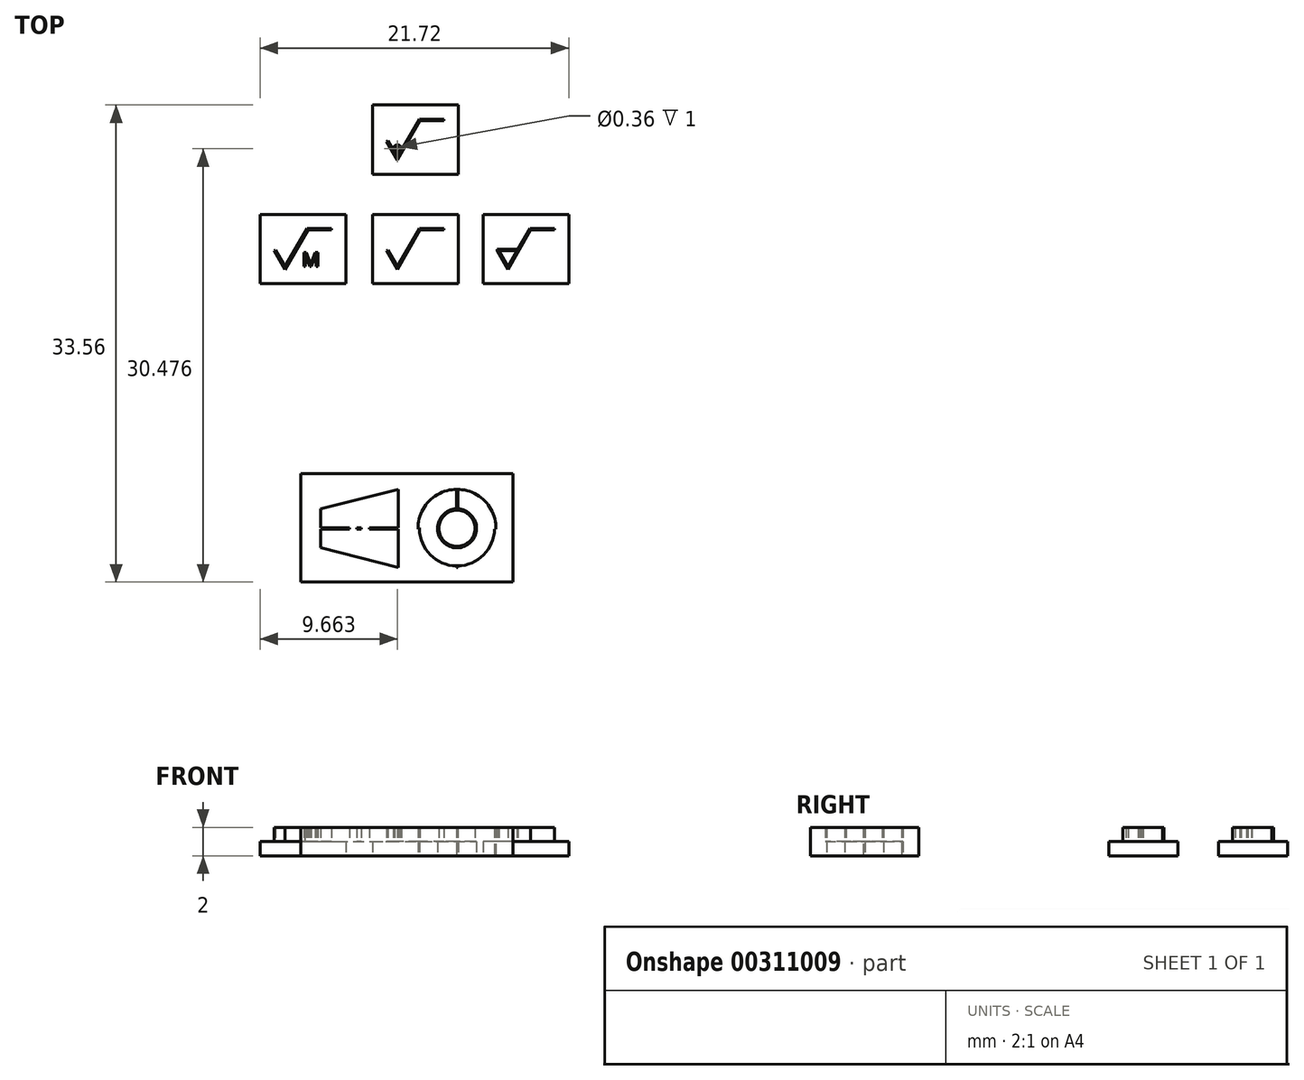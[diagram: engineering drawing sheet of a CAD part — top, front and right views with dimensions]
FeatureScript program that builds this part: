
annotation { "Feature Type Name" : "Feature", "Feature Type Description" : "" }
export const myFeature = defineFeature(function(context is Context, id is Id, definition is map)
    precondition{}
    {
        {
            var Q0;
            Q0=qCreatedBy(makeId("Top.planeOp"),FACE);
            var sketch = newSketch(context, id + "F0", { "sketchPlane" : qUnion([Q0])});
            skLineSegment(sketch, "E0", {"start": v(0, 0) * mm, "end": v(0, 277) * mm});
            skLineSegment(sketch, "E1", {"start": v(0, 277) * mm, "end": v(190, 277) * mm});
            skLineSegment(sketch, "E2", {"start": v(190, 277) * mm, "end": v(190, 0) * mm});
            skLineSegment(sketch, "E3", {"start": v(190, 0) * mm, "end": v(0, 0) * mm});
            skLineSegment(sketch, "E4", {"start": v(43, 0) * mm, "end": v(43, -9.5) * mm});
            skLineSegment(sketch, "E5", {"start": v(43, 277) * mm, "end": v(43, 286.5) * mm});
            skLineSegment(sketch, "E6", {"start": v(95, 0) * mm, "end": v(95, -9.5) * mm});
            skLineSegment(sketch, "E7", {"start": v(95, 277) * mm, "end": v(95, 286.5) * mm});
            skLineSegment(sketch, "E8", {"start": v(147, 0) * mm, "end": v(147, -9.5) * mm});
            skLineSegment(sketch, "E9", {"start": v(147, 277) * mm, "end": v(147, 286.5) * mm});
            skLineSegment(sketch, "E10", {"start": v(0, 40.5) * mm, "end": v(-9.5, 40.5) * mm});
            skLineSegment(sketch, "E11", {"start": v(190, 40.5) * mm, "end": v(199.5, 40.5) * mm});
            skLineSegment(sketch, "E12", {"start": v(0, 89.5) * mm, "end": v(-9.5, 89.5) * mm});
            skLineSegment(sketch, "E13", {"start": v(190, 89.5) * mm, "end": v(199.5, 89.5) * mm});
            skLineSegment(sketch, "E14", {"start": v(0, 138.5) * mm, "end": v(-9.5, 138.5) * mm});
            skLineSegment(sketch, "E15", {"start": v(190, 138.5) * mm, "end": v(199.5, 138.5) * mm});
            skLineSegment(sketch, "E16", {"start": v(0, 187.5) * mm, "end": v(-9.5, 187.5) * mm});
            skLineSegment(sketch, "E17", {"start": v(190, 187.5) * mm, "end": v(199.5, 187.5) * mm});
            skLineSegment(sketch, "E18", {"start": v(0, 236.5) * mm, "end": v(-9.5, 236.5) * mm});
            skLineSegment(sketch, "E19", {"start": v(190, 236.5) * mm, "end": v(199.5, 236.5) * mm});
            skLineSegment(sketch, "E20", {"start": v(28.08, 0) * mm, "end": v(28.08, 38.1) * mm});
            skLineSegment(sketch, "E21", {"start": v(28.08, 0) * mm, "end": v(58.56, 0) * mm});
            skLineSegment(sketch, "E22", {"start": v(28.08, 7.62) * mm, "end": v(58.56, 7.62) * mm});
            skLineSegment(sketch, "E23", {"start": v(28.08, 10.67) * mm, "end": v(58.56, 10.67) * mm});
            skLineSegment(sketch, "E24", {"start": v(28.08, 15.85) * mm, "end": v(58.56, 15.85) * mm});
            skLineSegment(sketch, "E25", {"start": v(28.08, 20.27) * mm, "end": v(58.56, 20.27) * mm});
            skLineSegment(sketch, "E26", {"start": v(28.08, 38.1) * mm, "end": v(58.56, 38.1) * mm});
            skLineSegment(sketch, "E27", {"start": v(41.8, 23.3) * mm, "end": v(42.55, 21.99) * mm});
            skLineSegment(sketch, "E28", {"start": v(42.55, 21.99) * mm, "end": v(44.15, 24.76) * mm});
            skLineSegment(sketch, "E29", {"start": v(44.15, 24.76) * mm, "end": v(45.83, 24.76) * mm});
            skCircle(sketch, "E30", {"center": v(46.74, 3.78) * mm, "radius": 1.37 * mm});
            skCircle(sketch, "E31", {"center": v(46.74, 3.78) * mm, "radius": 2.74 * mm});
            skLineSegment(sketch, "E32", {"start": v(47.43, 3.78) * mm, "end": v(46.06, 3.78) * mm, "construction": true});
            skLineSegment(sketch, "E33", {"start": v(46.74, 4.47) * mm, "end": v(46.74, 3.1) * mm, "construction": true});
            skLineSegment(sketch, "E34", {"start": v(48.12, 3.78) * mm, "end": v(50.17, 3.78) * mm, "construction": true});
            skLineSegment(sketch, "E35", {"start": v(46.74, 5.15) * mm, "end": v(46.74, 7.2) * mm});
            skLineSegment(sketch, "E36", {"start": v(45.37, 3.78) * mm, "end": v(43.31, 3.78) * mm, "construction": true});
            skLineSegment(sketch, "E37", {"start": v(46.74, 2.4) * mm, "end": v(46.74, 0.35) * mm, "construction": true});
            skLineSegment(sketch, "E38", {"start": v(42.63, 1.04) * mm, "end": v(42.63, 6.52) * mm});
            skLineSegment(sketch, "E39", {"start": v(42.63, 6.52) * mm, "end": v(37.14, 5.15) * mm});
            skLineSegment(sketch, "E40", {"start": v(37.14, 5.15) * mm, "end": v(37.14, 2.4) * mm});
            skLineSegment(sketch, "E41", {"start": v(37.14, 2.4) * mm, "end": v(42.63, 1.04) * mm});
            skLineSegment(sketch, "E42", {"start": v(40.57, 3.78) * mm, "end": v(42.97, 3.78) * mm, "construction": true});
            skLineSegment(sketch, "E43", {"start": v(40.02, 3.78) * mm, "end": v(39.68, 3.78) * mm, "construction": true});
            skLineSegment(sketch, "E44", {"start": v(39.2, 3.78) * mm, "end": v(36.8, 3.78) * mm, "construction": true});
            skLineSegment(sketch, "E45", {"start": v(58.56, 0) * mm, "end": v(58.56, 38.1) * mm});
            skLineSegment(sketch, "E46", {"start": v(71.9, 10.67) * mm, "end": v(71.9, 38.1) * mm});
            skLineSegment(sketch, "E47", {"start": v(87.13, 10.67) * mm, "end": v(87.13, 38.1) * mm});
            skLineSegment(sketch, "E48", {"start": v(85.22, 0) * mm, "end": v(85.22, 10.67) * mm});
            skLineSegment(sketch, "E49", {"start": v(102.37, 10.67) * mm, "end": v(102.37, 38.1) * mm});
            skLineSegment(sketch, "E50", {"start": v(58.56, 38.1) * mm, "end": v(111.9, 38.1) * mm});
            skLineSegment(sketch, "E51", {"start": v(58.56, 33.53) * mm, "end": v(111.9, 33.53) * mm});
            skLineSegment(sketch, "E52", {"start": v(58.56, 28.96) * mm, "end": v(111.9, 28.96) * mm});
            skLineSegment(sketch, "E53", {"start": v(58.56, 24.38) * mm, "end": v(111.9, 24.38) * mm});
            skLineSegment(sketch, "E54", {"start": v(58.56, 19.81) * mm, "end": v(111.9, 19.81) * mm});
            skLineSegment(sketch, "E55", {"start": v(58.56, 15.24) * mm, "end": v(111.9, 15.24) * mm});
            skLineSegment(sketch, "E56", {"start": v(58.56, 10.67) * mm, "end": v(111.9, 10.67) * mm});
            skLineSegment(sketch, "E57", {"start": v(111.9, 0) * mm, "end": v(111.9, 38.1) * mm});
            skLineSegment(sketch, "E58", {"start": v(121.42, 4.95) * mm, "end": v(121.42, 12.57) * mm});
            skLineSegment(sketch, "E59", {"start": v(128.66, 0) * mm, "end": v(128.66, 4.95) * mm});
            skLineSegment(sketch, "E60", {"start": v(163.33, 0) * mm, "end": v(163.33, 4.95) * mm});
            skLineSegment(sketch, "E61", {"start": v(182.38, 4.95) * mm, "end": v(182.38, 12.57) * mm});
            skLineSegment(sketch, "E62", {"start": v(111.9, 4.95) * mm, "end": v(190, 4.95) * mm});
            skLineSegment(sketch, "E63", {"start": v(111.9, 12.57) * mm, "end": v(190, 12.57) * mm});
            skLineSegment(sketch, "E64", {"start": v(111.9, 28.58) * mm, "end": v(190, 28.58) * mm});
            skLineSegment(sketch, "E65", {"start": v(111.9, 38.1) * mm, "end": v(190, 38.1) * mm});
            skLineSegment(sketch, "E66.0", {"start": v(42.73, 6.65) * mm, "end": v(37.04, 5.23) * mm});
            skLineSegment(sketch, "E66.1", {"start": v(42.73, 0.9) * mm, "end": v(42.73, 6.65) * mm});
            skLineSegment(sketch, "E66.2", {"start": v(37.04, 2.33) * mm, "end": v(42.73, 0.9) * mm});
            skLineSegment(sketch, "E66.3", {"start": v(37.04, 5.23) * mm, "end": v(37.04, 2.33) * mm});
            skLineSegment(sketch, "E67.bottom", {"start": v(39.2, 3.83) * mm, "end": v(36.8, 3.83) * mm});
            skLineSegment(sketch, "E67.top", {"start": v(39.2, 3.73) * mm, "end": v(36.8, 3.73) * mm});
            skLineSegment(sketch, "E67.left", {"start": v(39.2, 3.83) * mm, "end": v(39.2, 3.73) * mm});
            skLineSegment(sketch, "E67.right", {"start": v(36.8, 3.83) * mm, "end": v(36.8, 3.73) * mm});
            skPoint(sketch, "E67.middle", {"position": v(38, 3.78) * mm});
            skLineSegment(sketch, "E68", {"start": v(35.3, 5.15) * mm, "end": v(35.3, 2.4) * mm, "construction": true});
            skPoint(sketch, "E69", {"position": v(35.3, 3.78) * mm});
            skCircle(sketch, "E70.0", {"center": v(46.74, 3.78) * mm, "radius": 2.64 * mm});
            skCircle(sketch, "E71.0", {"center": v(46.74, 3.78) * mm, "radius": 1.27 * mm});
            skLineSegment(sketch, "E72.bottom", {"start": v(39.68, 3.83) * mm, "end": v(40.02, 3.83) * mm});
            skLineSegment(sketch, "E72.top", {"start": v(39.68, 3.73) * mm, "end": v(40.02, 3.73) * mm});
            skLineSegment(sketch, "E72.left", {"start": v(39.68, 3.83) * mm, "end": v(39.68, 3.73) * mm});
            skLineSegment(sketch, "E72.right", {"start": v(40.02, 3.83) * mm, "end": v(40.02, 3.73) * mm});
            skPoint(sketch, "E72.middle", {"position": v(39.85, 3.78) * mm});
            skLineSegment(sketch, "E73.bottom", {"start": v(42.97, 3.83) * mm, "end": v(40.57, 3.83) * mm});
            skLineSegment(sketch, "E73.top", {"start": v(42.97, 3.73) * mm, "end": v(40.57, 3.73) * mm});
            skLineSegment(sketch, "E73.left", {"start": v(42.97, 3.83) * mm, "end": v(42.97, 3.73) * mm});
            skLineSegment(sketch, "E73.right", {"start": v(40.57, 3.83) * mm, "end": v(40.57, 3.73) * mm});
            skPoint(sketch, "E73.middle", {"position": v(41.77, 3.78) * mm});
            skLineSegment(sketch, "E74.bottom", {"start": v(43.31, 3.83) * mm, "end": v(45.37, 3.83) * mm});
            skLineSegment(sketch, "E74.top", {"start": v(43.31, 3.73) * mm, "end": v(45.37, 3.73) * mm});
            skLineSegment(sketch, "E74.left", {"start": v(43.31, 3.83) * mm, "end": v(43.31, 3.73) * mm});
            skLineSegment(sketch, "E74.right", {"start": v(45.37, 3.83) * mm, "end": v(45.37, 3.73) * mm});
            skPoint(sketch, "E74.middle", {"position": v(44.34, 3.78) * mm});
            skLineSegment(sketch, "E75.bottom", {"start": v(47.43, 3.83) * mm, "end": v(46.06, 3.83) * mm});
            skLineSegment(sketch, "E75.top", {"start": v(47.43, 3.73) * mm, "end": v(46.06, 3.73) * mm});
            skLineSegment(sketch, "E75.left", {"start": v(47.43, 3.83) * mm, "end": v(47.43, 3.73) * mm});
            skLineSegment(sketch, "E75.right", {"start": v(46.06, 3.83) * mm, "end": v(46.06, 3.73) * mm});
            skLineSegment(sketch, "E76.bottom", {"start": v(46.8, 4.47) * mm, "end": v(46.7, 4.47) * mm});
            skLineSegment(sketch, "E76.top", {"start": v(46.8, 3.1) * mm, "end": v(46.7, 3.1) * mm});
            skLineSegment(sketch, "E76.left", {"start": v(46.8, 4.47) * mm, "end": v(46.8, 3.1) * mm});
            skLineSegment(sketch, "E76.right", {"start": v(46.7, 4.47) * mm, "end": v(46.7, 3.1) * mm});
            skLineSegment(sketch, "E77.bottom", {"start": v(46.8, 2.4) * mm, "end": v(46.7, 2.4) * mm});
            skLineSegment(sketch, "E77.top", {"start": v(46.8, 0.35) * mm, "end": v(46.7, 0.35) * mm});
            skLineSegment(sketch, "E77.left", {"start": v(46.8, 2.4) * mm, "end": v(46.8, 0.35) * mm});
            skLineSegment(sketch, "E77.right", {"start": v(46.7, 2.4) * mm, "end": v(46.7, 0.35) * mm});
            skPoint(sketch, "E77.middle", {"position": v(46.74, 1.38) * mm});
            skPoint(sketch, "E78", {"position": v(46.74, 6.18) * mm});
            skLineSegment(sketch, "E79.bottom", {"start": v(46.8, 5.15) * mm, "end": v(46.7, 5.15) * mm});
            skLineSegment(sketch, "E79.top", {"start": v(46.8, 7.2) * mm, "end": v(46.7, 7.2) * mm});
            skLineSegment(sketch, "E79.left", {"start": v(46.8, 5.15) * mm, "end": v(46.8, 7.2) * mm});
            skLineSegment(sketch, "E79.right", {"start": v(46.7, 5.15) * mm, "end": v(46.7, 7.2) * mm});
            skLineSegment(sketch, "E80.bottom", {"start": v(35.77, 7.62) * mm, "end": v(50.68, 7.62) * mm});
            skLineSegment(sketch, "E80.top", {"start": v(35.77, 0) * mm, "end": v(50.68, 0) * mm});
            skLineSegment(sketch, "E80.left", {"start": v(35.77, 7.62) * mm, "end": v(35.77, 0) * mm});
            skLineSegment(sketch, "E80.right", {"start": v(50.68, 7.62) * mm, "end": v(50.68, 0) * mm});
            skLineSegment(sketch, "E81.bottom", {"start": v(48.11, 3.83) * mm, "end": v(50.17, 3.83) * mm});
            skLineSegment(sketch, "E81.top", {"start": v(48.11, 3.73) * mm, "end": v(50.17, 3.73) * mm});
            skLineSegment(sketch, "E81.left", {"start": v(48.11, 3.83) * mm, "end": v(48.11, 3.73) * mm});
            skLineSegment(sketch, "E81.right", {"start": v(50.17, 3.83) * mm, "end": v(50.17, 3.73) * mm});
            skPoint(sketch, "E81.middle", {"position": v(49.14, 3.78) * mm});
            skLineSegment(sketch, "E82", {"start": v(41.8, 23.3) * mm, "end": v(41.88, 23.36) * mm});
            skLineSegment(sketch, "E83", {"start": v(41.88, 23.36) * mm, "end": v(42.55, 22.19) * mm});
            skLineSegment(sketch, "E84", {"start": v(42.55, 22.19) * mm, "end": v(44.15, 24.96) * mm});
            skLineSegment(sketch, "E85", {"start": v(44.15, 24.96) * mm, "end": v(45.83, 24.96) * mm, "construction": true});
            skLineSegment(sketch, "E86", {"start": v(45.83, 24.96) * mm, "end": v(45.83, 24.76) * mm});
            skLineSegment(sketch, "E87", {"start": v(45.83, 24.86) * mm, "end": v(44.1, 24.86) * mm});
            skPoint(sketch, "E88", {"position": v(50.33, 21.99) * mm});
            skLineSegment(sketch, "E89", {"start": v(49.57, 23.3) * mm, "end": v(50.33, 21.99) * mm});
            skLineSegment(sketch, "E90", {"start": v(50.33, 21.99) * mm, "end": v(51.93, 24.76) * mm});
            skLineSegment(sketch, "E91", {"start": v(51.93, 24.76) * mm, "end": v(53.6, 24.76) * mm});
            skLineSegment(sketch, "E92", {"start": v(49.57, 23.3) * mm, "end": v(49.65, 23.36) * mm, "construction": true});
            skLineSegment(sketch, "E93", {"start": v(49.65, 23.36) * mm, "end": v(50.33, 22.19) * mm});
            skLineSegment(sketch, "E94", {"start": v(50.33, 22.19) * mm, "end": v(51.93, 24.96) * mm});
            skLineSegment(sketch, "E95", {"start": v(51.93, 24.96) * mm, "end": v(53.6, 24.96) * mm, "construction": true});
            skLineSegment(sketch, "E96", {"start": v(53.6, 24.96) * mm, "end": v(53.6, 24.76) * mm});
            skLineSegment(sketch, "E97", {"start": v(53.6, 24.86) * mm, "end": v(51.87, 24.86) * mm});
            skPoint(sketch, "E98", {"position": v(49.57, 23.3) * mm});
            skPoint(sketch, "E99", {"position": v(51.1, 23.3) * mm});
            skLineSegment(sketch, "E100.bottom", {"start": v(49.57, 23.3) * mm, "end": v(51.1, 23.3) * mm});
            skLineSegment(sketch, "E100.top", {"start": v(49.57, 23.4) * mm, "end": v(51.1, 23.4) * mm});
            skLineSegment(sketch, "E100.left", {"start": v(49.57, 23.3) * mm, "end": v(49.57, 23.4) * mm});
            skLineSegment(sketch, "E100.right", {"start": v(51.1, 23.3) * mm, "end": v(51.1, 23.4) * mm});
            skPoint(sketch, "E101", {"position": v(40.8, 23.3) * mm});
            skPoint(sketch, "E102", {"position": v(45.83, 23.3) * mm});
            skPoint(sketch, "E103", {"position": v(46.83, 23.3) * mm});
            skPoint(sketch, "E104", {"position": v(42.55, 21.99) * mm});
            skPoint(sketch, "E105", {"position": v(42.55, 20.99) * mm});
            skPoint(sketch, "E106", {"position": v(44.1, 25.86) * mm});
            skLineSegment(sketch, "E107.bottom", {"start": v(40.8, 25.86) * mm, "end": v(46.83, 25.86) * mm});
            skLineSegment(sketch, "E107.top", {"start": v(40.8, 20.99) * mm, "end": v(46.83, 20.99) * mm});
            skLineSegment(sketch, "E107.left", {"start": v(40.8, 25.86) * mm, "end": v(40.8, 20.99) * mm});
            skLineSegment(sketch, "E107.right", {"start": v(46.83, 25.86) * mm, "end": v(46.83, 20.99) * mm});
            skLineSegment(sketch, "E108.bottom", {"start": v(54.6, 25.86) * mm, "end": v(48.57, 25.86) * mm});
            skLineSegment(sketch, "E108.top", {"start": v(54.6, 20.99) * mm, "end": v(48.57, 20.99) * mm});
            skLineSegment(sketch, "E108.left", {"start": v(54.6, 25.86) * mm, "end": v(54.6, 20.99) * mm});
            skLineSegment(sketch, "E108.right", {"start": v(48.57, 25.86) * mm, "end": v(48.57, 20.99) * mm});
            skPoint(sketch, "E109", {"position": v(40.8, 20.99) * mm});
            skLineSegment(sketch, "E110", {"start": v(33.9, 23.3) * mm, "end": v(34.65, 21.99) * mm});
            skLineSegment(sketch, "E111", {"start": v(34.65, 21.99) * mm, "end": v(36.25, 24.76) * mm});
            skLineSegment(sketch, "E112", {"start": v(36.25, 24.76) * mm, "end": v(37.93, 24.76) * mm});
            skLineSegment(sketch, "E113", {"start": v(33.9, 23.3) * mm, "end": v(33.98, 23.36) * mm});
            skLineSegment(sketch, "E114", {"start": v(33.98, 23.36) * mm, "end": v(34.65, 22.19) * mm});
            skLineSegment(sketch, "E115", {"start": v(34.65, 22.19) * mm, "end": v(36.25, 24.96) * mm});
            skLineSegment(sketch, "E116", {"start": v(36.25, 24.96) * mm, "end": v(37.93, 24.96) * mm, "construction": true});
            skLineSegment(sketch, "E117", {"start": v(37.93, 24.96) * mm, "end": v(37.93, 24.76) * mm});
            skLineSegment(sketch, "E118", {"start": v(37.93, 24.86) * mm, "end": v(36.2, 24.86) * mm});
            skPoint(sketch, "E119", {"position": v(32.9, 23.3) * mm});
            skPoint(sketch, "E120", {"position": v(37.93, 23.3) * mm});
            skPoint(sketch, "E121", {"position": v(38.93, 23.3) * mm});
            skPoint(sketch, "E122", {"position": v(34.65, 21.99) * mm});
            skPoint(sketch, "E123", {"position": v(34.65, 20.99) * mm});
            skPoint(sketch, "E124", {"position": v(36.2, 25.86) * mm});
            skLineSegment(sketch, "E125.bottom", {"start": v(32.9, 25.86) * mm, "end": v(38.93, 25.86) * mm});
            skLineSegment(sketch, "E125.top", {"start": v(32.9, 20.99) * mm, "end": v(38.93, 20.99) * mm});
            skLineSegment(sketch, "E125.left", {"start": v(32.9, 25.86) * mm, "end": v(32.9, 20.99) * mm});
            skLineSegment(sketch, "E125.right", {"start": v(38.93, 25.86) * mm, "end": v(38.93, 20.99) * mm});
            skPoint(sketch, "E126", {"position": v(32.9, 20.99) * mm});
            skText(sketch, "E127", { "text": "M", "fontName": "OpenSans-Regular.ttf"});
            skPoint(sketch, "E128", {"position": v(40.8, 28.7) * mm});
            skLineSegment(sketch, "E129", {"start": v(41.8, 31.01) * mm, "end": v(42.55, 29.7) * mm});
            skLineSegment(sketch, "E130", {"start": v(42.55, 29.7) * mm, "end": v(44.15, 32.46) * mm});
            skLineSegment(sketch, "E131", {"start": v(44.15, 32.46) * mm, "end": v(45.83, 32.46) * mm});
            skLineSegment(sketch, "E132", {"start": v(41.8, 31.01) * mm, "end": v(41.88, 31.06) * mm});
            skLineSegment(sketch, "E133", {"start": v(41.88, 31.06) * mm, "end": v(42.55, 29.9) * mm});
            skLineSegment(sketch, "E134", {"start": v(42.55, 29.9) * mm, "end": v(44.15, 32.66) * mm});
            skLineSegment(sketch, "E135", {"start": v(44.15, 32.66) * mm, "end": v(45.83, 32.66) * mm, "construction": true});
            skLineSegment(sketch, "E136", {"start": v(45.83, 32.66) * mm, "end": v(45.83, 32.46) * mm});
            skLineSegment(sketch, "E137", {"start": v(45.83, 32.56) * mm, "end": v(44.1, 32.56) * mm});
            skPoint(sketch, "E138", {"position": v(40.8, 31.01) * mm});
            skPoint(sketch, "E139", {"position": v(45.83, 31.01) * mm});
            skPoint(sketch, "E140", {"position": v(46.83, 31.01) * mm});
            skPoint(sketch, "E141", {"position": v(42.55, 29.7) * mm});
            skPoint(sketch, "E142", {"position": v(42.55, 28.7) * mm});
            skPoint(sketch, "E143", {"position": v(44.1, 33.56) * mm});
            skLineSegment(sketch, "E144.bottom", {"start": v(40.8, 33.56) * mm, "end": v(46.83, 33.56) * mm});
            skLineSegment(sketch, "E144.top", {"start": v(40.8, 28.7) * mm, "end": v(46.83, 28.7) * mm});
            skLineSegment(sketch, "E144.left", {"start": v(40.8, 33.56) * mm, "end": v(40.8, 28.7) * mm});
            skLineSegment(sketch, "E144.right", {"start": v(46.83, 33.56) * mm, "end": v(46.83, 28.7) * mm});
            skCircle(sketch, "E145", {"center": v(42.55, 30.48) * mm, "radius": 0.28 * mm});
            skPoint(sketch, "E145.centerSnap0", {"position": v(42.22, 30.48) * mm});
            skCircle(sketch, "E146", {"center": v(42.55, 30.48) * mm, "radius": 0.18 * mm});
            skPoint(sketch, "E147", {"position": v(42.8, 30.33) * mm});
            skLineSegment(sketch, "E148", {"start": v(42.44, 30.1) * mm, "end": v(42.55, 29.91) * mm});
            skLineSegment(sketch, "E149", {"start": v(42.55, 29.91) * mm, "end": v(42.68, 30.14) * mm});
            skLineSegment(sketch, "E150", {"start": v(42.55, 29.91) * mm, "end": v(43.07, 30.8) * mm, "construction": true});
            skLineSegment(sketch, "E151", {"start": v(42.55, 29.91) * mm, "end": v(42.12, 30.67) * mm, "construction": true});
            const initialGuessF0  = {"E127": [0.03583, 0.02219, 1, 0, 0.001]};
            skSetInitialGuess(sketch, initialGuessF0);
            skSolve(sketch);
        }
        {
            var Q0;
            {var subQ0=sQuery(id+"F0.wireOp",EDGE,"E79.left");var subQ5=sQuery(id+"F0.wireOp",EDGE,"E70.0");var subQ6=makeQuery(id+"F0.imprint","INTERSECT",VERTEX,{"derivedFrom":[subQ5,subQ0]});Q0=makeQuery(id+"F0.imprint","IMPRINT",FACE,{"disambiguationData":[TD([[makeQuery(id+"F0.imprint","IMPRINT",EDGE,{"disambiguationData":[TD([[subQ6,-1.0]])],"derivedFrom":subQ5}),-1.0]])]});}
            var Q1;
            Q1=makeQuery(id+"F0.imprint","IMPRINT",FACE,{"disambiguationData":[TD([[makeQuery(id+"F0.imprint","IMPRINT",EDGE,{"derivedFrom":sQuery(id+"F0.wireOp",EDGE,"E71.0")}),-1.0]])]});
            var Q2;
            {var subQ1=sQuery(id+"F0.wireOp",EDGE,"E74.bottom");var subQ5=sQuery(id+"F0.wireOp",EDGE,"E70.0");var subQ6=makeQuery(id+"F0.imprint","INTERSECT",VERTEX,{"derivedFrom":[subQ5,subQ1]});Q2=makeQuery(id+"F0.imprint","IMPRINT",FACE,{"disambiguationData":[TD([[makeQuery(id+"F0.imprint","IMPRINT",EDGE,{"disambiguationData":[TD([[subQ6,-1.0]])],"derivedFrom":subQ5}),-1.0]])]});}
            var Q3;
            {var subQ13=sQuery(id+"F0.wireOp",EDGE,"E39");Q3=makeQuery(id+"F0.imprint","IMPRINT",FACE,{"disambiguationData":[TD([[makeQuery(id+"F0.imprint","IMPRINT",EDGE,{"derivedFrom":subQ13}),1.0]])]});}
            var Q4;
            {var subQ0=sQuery(id+"F0.wireOp",EDGE,"E77.left");var subQ5=sQuery(id+"F0.wireOp",EDGE,"E70.0");var subQ6=makeQuery(id+"F0.imprint","INTERSECT",VERTEX,{"derivedFrom":[subQ5,subQ0]});Q4=makeQuery(id+"F0.imprint","IMPRINT",FACE,{"disambiguationData":[TD([[makeQuery(id+"F0.imprint","IMPRINT",EDGE,{"disambiguationData":[TD([[subQ6,1.0]])],"derivedFrom":subQ5}),-1.0]])]});}
            var Q5;
            {var subQ3=sQuery(id+"F0.wireOp",EDGE,"E30");var subQ9=sQuery(id+"F0.wireOp",EDGE,"E77.bottom");var subQ10=makeQuery(id+"F0.imprint","INTERSECT",VERTEX,{"derivedFrom":[subQ3,subQ9]});Q5=makeQuery(id+"F0.imprint","IMPRINT",FACE,{"disambiguationData":[TD([[makeQuery(id+"F0.imprint","IMPRINT",EDGE,{"disambiguationData":[TD([[subQ10,-1.0]])],"derivedFrom":subQ3}),1.0]])]});}
            var Q6;
            {var subQ1=sQuery(id+"F0.wireOp",EDGE,"E74.top");var subQ3=sQuery(id+"F0.wireOp",EDGE,"E70.0");var subQ4=makeQuery(id+"F0.imprint","INTERSECT",VERTEX,{"derivedFrom":[subQ3,subQ1]});Q6=makeQuery(id+"F0.imprint","IMPRINT",FACE,{"disambiguationData":[TD([[makeQuery(id+"F0.imprint","IMPRINT",EDGE,{"disambiguationData":[TD([[subQ4,-1.0]])],"derivedFrom":subQ3}),-1.0]])]});}
            var Q7;
            {var subQ0=sQuery(id+"F0.wireOp",EDGE,"E77.left");var subQ1=sQuery(id+"F0.wireOp",EDGE,"E31");var subQ2=makeQuery(id+"F0.imprint","INTERSECT",VERTEX,{"derivedFrom":[subQ1,subQ0]});Q7=makeQuery(id+"F0.imprint","IMPRINT",FACE,{"disambiguationData":[TD([[makeQuery(id+"F0.imprint","IMPRINT",EDGE,{"disambiguationData":[TD([[subQ2,1.0]])],"derivedFrom":subQ1}),-1.0]])]});}
            var Q8;
            {var subQ0=sQuery(id+"F0.wireOp",EDGE,"E74.bottom");var subQ1=sQuery(id+"F0.wireOp",EDGE,"E31");var subQ2=makeQuery(id+"F0.imprint","INTERSECT",VERTEX,{"derivedFrom":[subQ1,subQ0]});Q8=makeQuery(id+"F0.imprint","IMPRINT",FACE,{"disambiguationData":[TD([[makeQuery(id+"F0.imprint","IMPRINT",EDGE,{"disambiguationData":[TD([[subQ2,-1.0]])],"derivedFrom":subQ1}),-1.0]])]});}
            var Q9;
            {var subQ0=sQuery(id+"F0.wireOp",EDGE,"E67.bottom");var subQ1=sQuery(id+"F0.wireOp",EDGE,"E40");var subQ2=makeQuery(id+"F0.imprint","INTERSECT",VERTEX,{"derivedFrom":[subQ1,subQ0]});Q9=makeQuery(id+"F0.imprint","IMPRINT",FACE,{"disambiguationData":[TD([[makeQuery(id+"F0.imprint","IMPRINT",EDGE,{"disambiguationData":[TD([[subQ2,-1.0]])],"derivedFrom":subQ1}),-1.0]])]});}
            var Q10;
            {var subQ5=sQuery(id+"F0.wireOp",EDGE,"E74.left");Q10=makeQuery(id+"F0.imprint","IMPRINT",FACE,{"disambiguationData":[TD([[makeQuery(id+"F0.imprint","IMPRINT",EDGE,{"derivedFrom":subQ5}),1.0]])]});}
            var Q11;
            {var subQ1=sQuery(id+"F0.wireOp",EDGE,"E79.top");Q11=makeQuery(id+"F0.imprint","IMPRINT",FACE,{"disambiguationData":[TD([[makeQuery(id+"F0.imprint","IMPRINT",EDGE,{"derivedFrom":subQ1}),1.0]])]});}
            var Q12;
            {var subQ0=sQuery(id+"F0.wireOp",EDGE,"E35");var subQ1=sQuery(id+"F0.wireOp",EDGE,"E30");var subQ2=makeQuery(id+"F0.imprint","INTERSECT",VERTEX,{"derivedFrom":[subQ1,subQ0]});Q12=makeQuery(id+"F0.imprint","IMPRINT",FACE,{"disambiguationData":[TD([[makeQuery(id+"F0.imprint","IMPRINT",EDGE,{"disambiguationData":[TD([[subQ2,-1.0]])],"derivedFrom":subQ0}),1.0]])]});}
            var Q13;
            {var subQ0=sQuery(id+"F0.wireOp",EDGE,"E77.left");var subQ3=sQuery(id+"F0.wireOp",EDGE,"E70.0");var subQ4=makeQuery(id+"F0.imprint","INTERSECT",VERTEX,{"derivedFrom":[subQ3,subQ0]});Q13=makeQuery(id+"F0.imprint","IMPRINT",FACE,{"disambiguationData":[TD([[makeQuery(id+"F0.imprint","IMPRINT",EDGE,{"disambiguationData":[TD([[subQ4,-1.0]])],"derivedFrom":subQ3}),-1.0]])]});}
            var Q14;
            Q14=makeQuery(id+"F0.imprint","IMPRINT",FACE,{"disambiguationData":[TD([[makeQuery(id+"F0.imprint","IMPRINT",EDGE,{"derivedFrom":sQuery(id+"F0.wireOp",EDGE,"E71.0")}),1.0]])]});
            var Q15;
            {var subQ4=sQuery(id+"F0.wireOp",EDGE,"E81.top");var subQ6=sQuery(id+"F0.wireOp",EDGE,"E70.0");var subQ7=makeQuery(id+"F0.imprint","INTERSECT",VERTEX,{"derivedFrom":[subQ6,subQ4]});Q15=makeQuery(id+"F0.imprint","IMPRINT",FACE,{"disambiguationData":[TD([[makeQuery(id+"F0.imprint","IMPRINT",EDGE,{"disambiguationData":[TD([[subQ7,1.0]])],"derivedFrom":subQ6}),-1.0]])]});}
            var Q16;
            {var subQ0=sQuery(id+"F0.wireOp",EDGE,"E79.left");var subQ1=sQuery(id+"F0.wireOp",EDGE,"E31");var subQ2=makeQuery(id+"F0.imprint","INTERSECT",VERTEX,{"derivedFrom":[subQ1,subQ0]});Q16=makeQuery(id+"F0.imprint","IMPRINT",FACE,{"disambiguationData":[TD([[makeQuery(id+"F0.imprint","IMPRINT",EDGE,{"disambiguationData":[TD([[subQ2,-1.0]])],"derivedFrom":subQ1}),-1.0]])]});}
            var Q17;
            {var subQ0=sQuery(id+"F0.wireOp",EDGE,"E73.top");var subQ1=sQuery(id+"F0.wireOp",EDGE,"E38");var subQ2=makeQuery(id+"F0.imprint","INTERSECT",VERTEX,{"derivedFrom":[subQ1,subQ0]});Q17=makeQuery(id+"F0.imprint","IMPRINT",FACE,{"disambiguationData":[TD([[makeQuery(id+"F0.imprint","IMPRINT",EDGE,{"disambiguationData":[TD([[subQ2,-1.0]])],"derivedFrom":subQ1}),-1.0]])]});}
            var Q18;
            {var subQ0=sQuery(id+"F0.wireOp",EDGE,"E77.right");var subQ1=sQuery(id+"F0.wireOp",EDGE,"E31");var subQ2=makeQuery(id+"F0.imprint","INTERSECT",VERTEX,{"derivedFrom":[subQ1,subQ0]});Q18=makeQuery(id+"F0.imprint","IMPRINT",FACE,{"disambiguationData":[TD([[makeQuery(id+"F0.imprint","IMPRINT",EDGE,{"disambiguationData":[TD([[subQ2,-1.0]])],"derivedFrom":subQ1}),-1.0]])]});}
            var Q19;
            {var subQ1=sQuery(id+"F0.wireOp",EDGE,"E39");Q19=makeQuery(id+"F0.imprint","IMPRINT",FACE,{"disambiguationData":[TD([[makeQuery(id+"F0.imprint","IMPRINT",EDGE,{"derivedFrom":subQ1}),-1.0]])]});}
            var Q20;
            {var subQ0=sQuery(id+"F0.wireOp",EDGE,"E75.left");Q20=makeQuery(id+"F0.imprint","IMPRINT",FACE,{"disambiguationData":[TD([[makeQuery(id+"F0.imprint","IMPRINT",EDGE,{"derivedFrom":subQ0}),-1.0]])]});}
            var Q21;
            {var subQ5=sQuery(id+"F0.wireOp",EDGE,"E67.left");Q21=makeQuery(id+"F0.imprint","IMPRINT",FACE,{"disambiguationData":[TD([[makeQuery(id+"F0.imprint","IMPRINT",EDGE,{"derivedFrom":subQ5}),-1.0]])]});}
            var Q22;
            {var subQ5=sQuery(id+"F0.wireOp",EDGE,"E73.right");Q22=makeQuery(id+"F0.imprint","IMPRINT",FACE,{"disambiguationData":[TD([[makeQuery(id+"F0.imprint","IMPRINT",EDGE,{"derivedFrom":subQ5}),1.0]])]});}
            var Q23;
            {var subQ5=sQuery(id+"F0.wireOp",EDGE,"E81.right");Q23=makeQuery(id+"F0.imprint","IMPRINT",FACE,{"disambiguationData":[TD([[makeQuery(id+"F0.imprint","IMPRINT",EDGE,{"derivedFrom":subQ5}),-1.0]])]});}
            var Q24;
            {var subQ0=sQuery(id+"F0.wireOp",EDGE,"E41");Q24=makeQuery(id+"F0.imprint","IMPRINT",FACE,{"disambiguationData":[TD([[makeQuery(id+"F0.imprint","IMPRINT",EDGE,{"derivedFrom":subQ0}),-1.0]])]});}
            var Q25;
            {var subQ0=sQuery(id+"F0.wireOp",EDGE,"E35");var subQ1=sQuery(id+"F0.wireOp",EDGE,"E30");var subQ2=makeQuery(id+"F0.imprint","INTERSECT",VERTEX,{"derivedFrom":[subQ1,subQ0]});Q25=makeQuery(id+"F0.imprint","IMPRINT",FACE,{"disambiguationData":[TD([[makeQuery(id+"F0.imprint","IMPRINT",EDGE,{"disambiguationData":[TD([[subQ2,-1.0]])],"derivedFrom":subQ0}),-1.0]])]});}
            var Q26;
            {var subQ0=sQuery(id+"F0.wireOp",EDGE,"E35");var subQ1=sQuery(id+"F0.wireOp",EDGE,"E31");var subQ2=makeQuery(id+"F0.imprint","INTERSECT",VERTEX,{"derivedFrom":[subQ1,subQ0]});Q26=makeQuery(id+"F0.imprint","IMPRINT",FACE,{"disambiguationData":[TD([[makeQuery(id+"F0.imprint","IMPRINT",EDGE,{"disambiguationData":[TD([[subQ2,1.0]])],"derivedFrom":subQ1}),-1.0]])]});}
            var Q27;
            {var subQ5=sQuery(id+"F0.wireOp",EDGE,"E77.top");Q27=makeQuery(id+"F0.imprint","IMPRINT",FACE,{"disambiguationData":[TD([[makeQuery(id+"F0.imprint","IMPRINT",EDGE,{"derivedFrom":subQ5}),-1.0]])]});}
            var Q28;
            {var subQ0=sQuery(id+"F0.wireOp",EDGE,"E81.top");var subQ1=sQuery(id+"F0.wireOp",EDGE,"E31");var subQ2=makeQuery(id+"F0.imprint","INTERSECT",VERTEX,{"derivedFrom":[subQ1,subQ0]});Q28=makeQuery(id+"F0.imprint","IMPRINT",FACE,{"disambiguationData":[TD([[makeQuery(id+"F0.imprint","IMPRINT",EDGE,{"disambiguationData":[TD([[subQ2,1.0]])],"derivedFrom":subQ1}),-1.0]])]});}
            var Q29;
            {var subQ0=sQuery(id+"F0.wireOp",EDGE,"E77.left");var subQ1=sQuery(id+"F0.wireOp",EDGE,"E31");var subQ2=makeQuery(id+"F0.imprint","INTERSECT",VERTEX,{"derivedFrom":[subQ1,subQ0]});Q29=makeQuery(id+"F0.imprint","IMPRINT",FACE,{"disambiguationData":[TD([[makeQuery(id+"F0.imprint","IMPRINT",EDGE,{"disambiguationData":[TD([[subQ2,-1.0]])],"derivedFrom":subQ1}),-1.0]])]});}
            var Q30;
            {var subQ5=sQuery(id+"F0.wireOp",EDGE,"E73.left");Q30=makeQuery(id+"F0.imprint","IMPRINT",FACE,{"disambiguationData":[TD([[makeQuery(id+"F0.imprint","IMPRINT",EDGE,{"derivedFrom":subQ5}),-1.0]])]});}
            var Q31;
            {var subQ5=sQuery(id+"F0.wireOp",EDGE,"E76.top");Q31=makeQuery(id+"F0.imprint","IMPRINT",FACE,{"disambiguationData":[TD([[makeQuery(id+"F0.imprint","IMPRINT",EDGE,{"derivedFrom":subQ5}),-1.0]])]});}
            var Q32;
            {var subQ0=sQuery(id+"F0.wireOp",EDGE,"E74.top");var subQ1=sQuery(id+"F0.wireOp",EDGE,"E31");var subQ2=makeQuery(id+"F0.imprint","INTERSECT",VERTEX,{"derivedFrom":[subQ1,subQ0]});Q32=makeQuery(id+"F0.imprint","IMPRINT",FACE,{"disambiguationData":[TD([[makeQuery(id+"F0.imprint","IMPRINT",EDGE,{"disambiguationData":[TD([[subQ2,-1.0]])],"derivedFrom":subQ1}),-1.0]])]});}
            var Q33;
            {var subQ5=sQuery(id+"F0.wireOp",EDGE,"E76.bottom");Q33=makeQuery(id+"F0.imprint","IMPRINT",FACE,{"disambiguationData":[TD([[makeQuery(id+"F0.imprint","IMPRINT",EDGE,{"derivedFrom":subQ5}),1.0]])]});}
            var Q34;
            {var subQ0=sQuery(id+"F0.wireOp",EDGE,"E35");var subQ1=sQuery(id+"F0.wireOp",EDGE,"E31");var subQ2=makeQuery(id+"F0.imprint","INTERSECT",VERTEX,{"derivedFrom":[subQ1,subQ0]});Q34=makeQuery(id+"F0.imprint","IMPRINT",FACE,{"disambiguationData":[TD([[makeQuery(id+"F0.imprint","IMPRINT",EDGE,{"disambiguationData":[TD([[subQ2,-1.0]])],"derivedFrom":subQ1}),-1.0]])]});}
            var Q35;
            {var subQ5=sQuery(id+"F0.wireOp",EDGE,"E67.right");Q35=makeQuery(id+"F0.imprint","IMPRINT",FACE,{"disambiguationData":[TD([[makeQuery(id+"F0.imprint","IMPRINT",EDGE,{"derivedFrom":subQ5}),1.0]])]});}
            var Q36;
            {var subQ0=sQuery(id+"F0.wireOp",EDGE,"E75.right");Q36=makeQuery(id+"F0.imprint","IMPRINT",FACE,{"disambiguationData":[TD([[makeQuery(id+"F0.imprint","IMPRINT",EDGE,{"derivedFrom":subQ0}),1.0]])]});}
            var Q37;
            {var subQ2=sQuery(id+"F0.wireOp",EDGE,"E79.bottom");Q37=makeQuery(id+"F0.imprint","IMPRINT",FACE,{"disambiguationData":[TD([[makeQuery(id+"F0.imprint","IMPRINT",EDGE,{"derivedFrom":subQ2}),-1.0]])]});}
            var Q38;
            {var subQ0=sQuery(id+"F0.wireOp",EDGE,"E81.left");Q38=makeQuery(id+"F0.imprint","IMPRINT",FACE,{"disambiguationData":[TD([[makeQuery(id+"F0.imprint","IMPRINT",EDGE,{"derivedFrom":subQ0}),1.0]])]});}
            var Q39;
            Q39=makeQuery(id+"F0.imprint","IMPRINT",FACE,{"disambiguationData":[TD([[makeQuery(id+"F0.imprint","IMPRINT",EDGE,{"derivedFrom":sQuery(id+"F0.wireOp",EDGE,"E72.bottom")}),-1.0]])]});
            var Q40;
            {var subQ0=sQuery(id+"F0.wireOp",EDGE,"E76.left");var subQ1=sQuery(id+"F0.wireOp",EDGE,"E75.bottom");var subQ2=makeQuery(id+"F0.imprint","INTERSECT",VERTEX,{"derivedFrom":[subQ1,subQ0]});Q40=makeQuery(id+"F0.imprint","IMPRINT",FACE,{"disambiguationData":[TD([[makeQuery(id+"F0.imprint","IMPRINT",EDGE,{"disambiguationData":[TD([[subQ2,-1.0]])],"derivedFrom":subQ1}),1.0]])]});}
            var Q41;
            {var subQ28=sQuery(id+"F0.wireOp",EDGE,"E66.0");Q41=makeQuery(id+"F0.imprint","IMPRINT",FACE,{"disambiguationData":[TD([[makeQuery(id+"F0.imprint","IMPRINT",EDGE,{"derivedFrom":subQ28}),-1.0]])]});}
            extrude(context, id + "F1", {"entities" : qUnion([Q0, Q1, Q2, Q3, Q4, Q5, Q6, Q7, Q8, Q9, Q10, Q11, Q12, Q13, Q14, Q15, Q16, Q17, Q18, Q19, Q20, Q21, Q22, Q23, Q24, Q25, Q26, Q27, Q28, Q29, Q30, Q31, Q32, Q33, Q34, Q35, Q36, Q37, Q38, Q39, Q40, Q41]), "depth" : 1 * mm});
        }
        {
            var Q0;
            {var subQ0=sQuery(id+"F0.wireOp",EDGE,"E41");Q0=makeQuery(id+"F0.imprint","IMPRINT",FACE,{"disambiguationData":[TD([[makeQuery(id+"F0.imprint","IMPRINT",EDGE,{"derivedFrom":subQ0}),-1.0]])]});}
            var Q1;
            {var subQ1=sQuery(id+"F0.wireOp",EDGE,"E39");Q1=makeQuery(id+"F0.imprint","IMPRINT",FACE,{"disambiguationData":[TD([[makeQuery(id+"F0.imprint","IMPRINT",EDGE,{"derivedFrom":subQ1}),-1.0]])]});}
            var Q2;
            {var subQ5=sQuery(id+"F0.wireOp",EDGE,"E73.right");Q2=makeQuery(id+"F0.imprint","IMPRINT",FACE,{"disambiguationData":[TD([[makeQuery(id+"F0.imprint","IMPRINT",EDGE,{"derivedFrom":subQ5}),1.0]])]});}
            var Q3;
            {var subQ5=sQuery(id+"F0.wireOp",EDGE,"E73.left");Q3=makeQuery(id+"F0.imprint","IMPRINT",FACE,{"disambiguationData":[TD([[makeQuery(id+"F0.imprint","IMPRINT",EDGE,{"derivedFrom":subQ5}),-1.0]])]});}
            var Q4;
            {var subQ0=sQuery(id+"F0.wireOp",EDGE,"E73.top");var subQ1=sQuery(id+"F0.wireOp",EDGE,"E38");var subQ2=makeQuery(id+"F0.imprint","INTERSECT",VERTEX,{"derivedFrom":[subQ1,subQ0]});Q4=makeQuery(id+"F0.imprint","IMPRINT",FACE,{"disambiguationData":[TD([[makeQuery(id+"F0.imprint","IMPRINT",EDGE,{"disambiguationData":[TD([[subQ2,-1.0]])],"derivedFrom":subQ1}),-1.0]])]});}
            var Q5;
            {var subQ5=sQuery(id+"F0.wireOp",EDGE,"E67.left");Q5=makeQuery(id+"F0.imprint","IMPRINT",FACE,{"disambiguationData":[TD([[makeQuery(id+"F0.imprint","IMPRINT",EDGE,{"derivedFrom":subQ5}),-1.0]])]});}
            var Q6;
            {var subQ0=sQuery(id+"F0.wireOp",EDGE,"E67.bottom");var subQ1=sQuery(id+"F0.wireOp",EDGE,"E40");var subQ2=makeQuery(id+"F0.imprint","INTERSECT",VERTEX,{"derivedFrom":[subQ1,subQ0]});Q6=makeQuery(id+"F0.imprint","IMPRINT",FACE,{"disambiguationData":[TD([[makeQuery(id+"F0.imprint","IMPRINT",EDGE,{"disambiguationData":[TD([[subQ2,-1.0]])],"derivedFrom":subQ1}),-1.0]])]});}
            var Q7;
            {var subQ5=sQuery(id+"F0.wireOp",EDGE,"E67.right");Q7=makeQuery(id+"F0.imprint","IMPRINT",FACE,{"disambiguationData":[TD([[makeQuery(id+"F0.imprint","IMPRINT",EDGE,{"derivedFrom":subQ5}),1.0]])]});}
            var Q8;
            Q8=makeQuery(id+"F0.imprint","IMPRINT",FACE,{"disambiguationData":[TD([[makeQuery(id+"F0.imprint","IMPRINT",EDGE,{"derivedFrom":sQuery(id+"F0.wireOp",EDGE,"E72.bottom")}),-1.0]])]});
            var Q9;
            Q9=makeQuery(id+"F0.imprint","IMPRINT",FACE,{"disambiguationData":[TD([[makeQuery(id+"F0.imprint","IMPRINT",EDGE,{"derivedFrom":sQuery(id+"F0.wireOp",EDGE,"E71.0")}),1.0]])]});
            var Q10;
            {var subQ1=sQuery(id+"F0.wireOp",EDGE,"E74.top");var subQ3=sQuery(id+"F0.wireOp",EDGE,"E70.0");var subQ4=makeQuery(id+"F0.imprint","INTERSECT",VERTEX,{"derivedFrom":[subQ3,subQ1]});Q10=makeQuery(id+"F0.imprint","IMPRINT",FACE,{"disambiguationData":[TD([[makeQuery(id+"F0.imprint","IMPRINT",EDGE,{"disambiguationData":[TD([[subQ4,-1.0]])],"derivedFrom":subQ3}),-1.0]])]});}
            var Q11;
            {var subQ0=sQuery(id+"F0.wireOp",EDGE,"E74.top");var subQ1=sQuery(id+"F0.wireOp",EDGE,"E31");var subQ2=makeQuery(id+"F0.imprint","INTERSECT",VERTEX,{"derivedFrom":[subQ1,subQ0]});Q11=makeQuery(id+"F0.imprint","IMPRINT",FACE,{"disambiguationData":[TD([[makeQuery(id+"F0.imprint","IMPRINT",EDGE,{"disambiguationData":[TD([[subQ2,-1.0]])],"derivedFrom":subQ1}),-1.0]])]});}
            var Q12;
            {var subQ5=sQuery(id+"F0.wireOp",EDGE,"E74.left");Q12=makeQuery(id+"F0.imprint","IMPRINT",FACE,{"disambiguationData":[TD([[makeQuery(id+"F0.imprint","IMPRINT",EDGE,{"derivedFrom":subQ5}),1.0]])]});}
            var Q13;
            {var subQ0=sQuery(id+"F0.wireOp",EDGE,"E74.bottom");var subQ1=sQuery(id+"F0.wireOp",EDGE,"E31");var subQ2=makeQuery(id+"F0.imprint","INTERSECT",VERTEX,{"derivedFrom":[subQ1,subQ0]});Q13=makeQuery(id+"F0.imprint","IMPRINT",FACE,{"disambiguationData":[TD([[makeQuery(id+"F0.imprint","IMPRINT",EDGE,{"disambiguationData":[TD([[subQ2,-1.0]])],"derivedFrom":subQ1}),-1.0]])]});}
            var Q14;
            {var subQ0=sQuery(id+"F0.wireOp",EDGE,"E77.left");var subQ1=sQuery(id+"F0.wireOp",EDGE,"E31");var subQ2=makeQuery(id+"F0.imprint","INTERSECT",VERTEX,{"derivedFrom":[subQ1,subQ0]});Q14=makeQuery(id+"F0.imprint","IMPRINT",FACE,{"disambiguationData":[TD([[makeQuery(id+"F0.imprint","IMPRINT",EDGE,{"disambiguationData":[TD([[subQ2,-1.0]])],"derivedFrom":subQ1}),-1.0]])]});}
            var Q15;
            {var subQ0=sQuery(id+"F0.wireOp",EDGE,"E77.right");var subQ1=sQuery(id+"F0.wireOp",EDGE,"E31");var subQ2=makeQuery(id+"F0.imprint","INTERSECT",VERTEX,{"derivedFrom":[subQ1,subQ0]});Q15=makeQuery(id+"F0.imprint","IMPRINT",FACE,{"disambiguationData":[TD([[makeQuery(id+"F0.imprint","IMPRINT",EDGE,{"disambiguationData":[TD([[subQ2,-1.0]])],"derivedFrom":subQ1}),-1.0]])]});}
            var Q16;
            {var subQ0=sQuery(id+"F0.wireOp",EDGE,"E77.left");var subQ1=sQuery(id+"F0.wireOp",EDGE,"E31");var subQ2=makeQuery(id+"F0.imprint","INTERSECT",VERTEX,{"derivedFrom":[subQ1,subQ0]});Q16=makeQuery(id+"F0.imprint","IMPRINT",FACE,{"disambiguationData":[TD([[makeQuery(id+"F0.imprint","IMPRINT",EDGE,{"disambiguationData":[TD([[subQ2,1.0]])],"derivedFrom":subQ1}),-1.0]])]});}
            var Q17;
            {var subQ0=sQuery(id+"F0.wireOp",EDGE,"E77.left");var subQ3=sQuery(id+"F0.wireOp",EDGE,"E70.0");var subQ4=makeQuery(id+"F0.imprint","INTERSECT",VERTEX,{"derivedFrom":[subQ3,subQ0]});Q17=makeQuery(id+"F0.imprint","IMPRINT",FACE,{"disambiguationData":[TD([[makeQuery(id+"F0.imprint","IMPRINT",EDGE,{"disambiguationData":[TD([[subQ4,-1.0]])],"derivedFrom":subQ3}),-1.0]])]});}
            var Q18;
            {var subQ0=sQuery(id+"F0.wireOp",EDGE,"E79.left");var subQ1=sQuery(id+"F0.wireOp",EDGE,"E31");var subQ2=makeQuery(id+"F0.imprint","INTERSECT",VERTEX,{"derivedFrom":[subQ1,subQ0]});Q18=makeQuery(id+"F0.imprint","IMPRINT",FACE,{"disambiguationData":[TD([[makeQuery(id+"F0.imprint","IMPRINT",EDGE,{"disambiguationData":[TD([[subQ2,-1.0]])],"derivedFrom":subQ1}),-1.0]])]});}
            var Q19;
            {var subQ1=sQuery(id+"F0.wireOp",EDGE,"E79.top");Q19=makeQuery(id+"F0.imprint","IMPRINT",FACE,{"disambiguationData":[TD([[makeQuery(id+"F0.imprint","IMPRINT",EDGE,{"derivedFrom":subQ1}),1.0]])]});}
            var Q20;
            {var subQ0=sQuery(id+"F0.wireOp",EDGE,"E35");var subQ1=sQuery(id+"F0.wireOp",EDGE,"E31");var subQ2=makeQuery(id+"F0.imprint","INTERSECT",VERTEX,{"derivedFrom":[subQ1,subQ0]});Q20=makeQuery(id+"F0.imprint","IMPRINT",FACE,{"disambiguationData":[TD([[makeQuery(id+"F0.imprint","IMPRINT",EDGE,{"disambiguationData":[TD([[subQ2,1.0]])],"derivedFrom":subQ1}),-1.0]])]});}
            var Q21;
            {var subQ0=sQuery(id+"F0.wireOp",EDGE,"E35");var subQ1=sQuery(id+"F0.wireOp",EDGE,"E31");var subQ2=makeQuery(id+"F0.imprint","INTERSECT",VERTEX,{"derivedFrom":[subQ1,subQ0]});Q21=makeQuery(id+"F0.imprint","IMPRINT",FACE,{"disambiguationData":[TD([[makeQuery(id+"F0.imprint","IMPRINT",EDGE,{"disambiguationData":[TD([[subQ2,-1.0]])],"derivedFrom":subQ1}),-1.0]])]});}
            var Q22;
            {var subQ5=sQuery(id+"F0.wireOp",EDGE,"E81.right");Q22=makeQuery(id+"F0.imprint","IMPRINT",FACE,{"disambiguationData":[TD([[makeQuery(id+"F0.imprint","IMPRINT",EDGE,{"derivedFrom":subQ5}),-1.0]])]});}
            var Q23;
            {var subQ0=sQuery(id+"F0.wireOp",EDGE,"E81.top");var subQ1=sQuery(id+"F0.wireOp",EDGE,"E31");var subQ2=makeQuery(id+"F0.imprint","INTERSECT",VERTEX,{"derivedFrom":[subQ1,subQ0]});Q23=makeQuery(id+"F0.imprint","IMPRINT",FACE,{"disambiguationData":[TD([[makeQuery(id+"F0.imprint","IMPRINT",EDGE,{"disambiguationData":[TD([[subQ2,1.0]])],"derivedFrom":subQ1}),-1.0]])]});}
            var Q24;
            {var subQ4=sQuery(id+"F0.wireOp",EDGE,"E81.top");var subQ6=sQuery(id+"F0.wireOp",EDGE,"E70.0");var subQ7=makeQuery(id+"F0.imprint","INTERSECT",VERTEX,{"derivedFrom":[subQ6,subQ4]});Q24=makeQuery(id+"F0.imprint","IMPRINT",FACE,{"disambiguationData":[TD([[makeQuery(id+"F0.imprint","IMPRINT",EDGE,{"disambiguationData":[TD([[subQ7,1.0]])],"derivedFrom":subQ6}),-1.0]])]});}
            var Q25;
            {var subQ0=sQuery(id+"F0.wireOp",EDGE,"E75.left");Q25=makeQuery(id+"F0.imprint","IMPRINT",FACE,{"disambiguationData":[TD([[makeQuery(id+"F0.imprint","IMPRINT",EDGE,{"derivedFrom":subQ0}),-1.0]])]});}
            var Q26;
            {var subQ0=sQuery(id+"F0.wireOp",EDGE,"E75.right");Q26=makeQuery(id+"F0.imprint","IMPRINT",FACE,{"disambiguationData":[TD([[makeQuery(id+"F0.imprint","IMPRINT",EDGE,{"derivedFrom":subQ0}),1.0]])]});}
            var Q27;
            {var subQ5=sQuery(id+"F0.wireOp",EDGE,"E76.bottom");Q27=makeQuery(id+"F0.imprint","IMPRINT",FACE,{"disambiguationData":[TD([[makeQuery(id+"F0.imprint","IMPRINT",EDGE,{"derivedFrom":subQ5}),1.0]])]});}
            var Q28;
            {var subQ5=sQuery(id+"F0.wireOp",EDGE,"E76.top");Q28=makeQuery(id+"F0.imprint","IMPRINT",FACE,{"disambiguationData":[TD([[makeQuery(id+"F0.imprint","IMPRINT",EDGE,{"derivedFrom":subQ5}),-1.0]])]});}
            var Q29;
            {var subQ0=sQuery(id+"F0.wireOp",EDGE,"E76.left");var subQ1=sQuery(id+"F0.wireOp",EDGE,"E75.bottom");var subQ2=makeQuery(id+"F0.imprint","INTERSECT",VERTEX,{"derivedFrom":[subQ1,subQ0]});Q29=makeQuery(id+"F0.imprint","IMPRINT",FACE,{"disambiguationData":[TD([[makeQuery(id+"F0.imprint","IMPRINT",EDGE,{"disambiguationData":[TD([[subQ2,-1.0]])],"derivedFrom":subQ1}),1.0]])]});}
            var Q30;
            {var subQ5=sQuery(id+"F0.wireOp",EDGE,"E77.top");Q30=makeQuery(id+"F0.imprint","IMPRINT",FACE,{"disambiguationData":[TD([[makeQuery(id+"F0.imprint","IMPRINT",EDGE,{"derivedFrom":subQ5}),-1.0]])]});}
            var Q31;
            {var subQ0=sQuery(id+"F0.wireOp",EDGE,"E35");var subQ1=sQuery(id+"F0.wireOp",EDGE,"E30");var subQ2=makeQuery(id+"F0.imprint","INTERSECT",VERTEX,{"derivedFrom":[subQ1,subQ0]});Q31=makeQuery(id+"F0.imprint","IMPRINT",FACE,{"disambiguationData":[TD([[makeQuery(id+"F0.imprint","IMPRINT",EDGE,{"disambiguationData":[TD([[subQ2,-1.0]])],"derivedFrom":subQ0}),-1.0]])]});}
            var Q32;
            {var subQ0=sQuery(id+"F0.wireOp",EDGE,"E35");var subQ1=sQuery(id+"F0.wireOp",EDGE,"E30");var subQ2=makeQuery(id+"F0.imprint","INTERSECT",VERTEX,{"derivedFrom":[subQ1,subQ0]});Q32=makeQuery(id+"F0.imprint","IMPRINT",FACE,{"disambiguationData":[TD([[makeQuery(id+"F0.imprint","IMPRINT",EDGE,{"disambiguationData":[TD([[subQ2,-1.0]])],"derivedFrom":subQ0}),1.0]])]});}
            extrude(context, id + "F2", {"entities" : qUnion([Q0, Q1, Q2, Q3, Q4, Q5, Q6, Q7, Q8, Q9, Q10, Q11, Q12, Q13, Q14, Q15, Q16, Q17, Q18, Q19, Q20, Q21, Q22, Q23, Q24, Q25, Q26, Q27, Q28, Q29, Q30, Q31, Q32]), "operationType" : NewBodyOperationType.ADD, "depth" : 2 * mm});
        }
        {
            var Q0;
            Q0=makeQuery(id+"F0.imprint","IMPRINT",FACE,{"disambiguationData":[TD([[makeQuery(id+"F0.imprint","IMPRINT",EDGE,{"derivedFrom":sQuery(id+"F0.wireOp",EDGE,"E27")}),-1.0]])]});
            var Q1;
            Q1=makeQuery(id+"F0.imprint","IMPRINT",FACE,{"disambiguationData":[TD([[makeQuery(id+"F0.imprint","IMPRINT",EDGE,{"derivedFrom":sQuery(id+"F0.wireOp",EDGE,"E27")}),1.0]])]});
            var Q2;
            {var subQ7=sQuery(id+"F0.wireOp",EDGE,"E89");Q2=makeQuery(id+"F0.imprint","IMPRINT",FACE,{"disambiguationData":[TD([[makeQuery(id+"F0.imprint","IMPRINT",EDGE,{"derivedFrom":subQ7}),-1.0]])]});}
            var Q3;
            {var subQ6=sQuery(id+"F0.wireOp",EDGE,"E89");Q3=makeQuery(id+"F0.imprint","IMPRINT",FACE,{"disambiguationData":[TD([[makeQuery(id+"F0.imprint","IMPRINT",EDGE,{"derivedFrom":subQ6}),1.0]])]});}
            var Q4;
            {var subQ0=sQuery(id+"F0.wireOp",EDGE,"E94");var subQ1=sQuery(id+"F0.wireOp",EDGE,"E93");var subQ2=makeQuery(id+"F0.imprint","INTERSECT",VERTEX,{"derivedFrom":[subQ1,subQ0]});Q4=makeQuery(id+"F0.imprint","IMPRINT",FACE,{"disambiguationData":[TD([[makeQuery(id+"F0.imprint","IMPRINT",EDGE,{"disambiguationData":[TD([[subQ2,1.0]])],"derivedFrom":subQ1}),1.0]])]});}
            var Q5;
            {var subQ0=sQuery(id+"F0.wireOp",EDGE,"E100.left");Q5=makeQuery(id+"F0.imprint","IMPRINT",FACE,{"disambiguationData":[TD([[makeQuery(id+"F0.imprint","IMPRINT",EDGE,{"derivedFrom":subQ0}),-1.0]])]});}
            var Q6;
            {var subQ1=sQuery(id+"F0.wireOp",EDGE,"E91");Q6=makeQuery(id+"F0.imprint","IMPRINT",FACE,{"disambiguationData":[TD([[makeQuery(id+"F0.imprint","IMPRINT",EDGE,{"derivedFrom":subQ1}),1.0]])]});}
            var Q7;
            {var subQ5=sQuery(id+"F0.wireOp",EDGE,"E100.right");Q7=makeQuery(id+"F0.imprint","IMPRINT",FACE,{"disambiguationData":[TD([[makeQuery(id+"F0.imprint","IMPRINT",EDGE,{"derivedFrom":subQ5}),1.0]])]});}
            var Q8;
            Q8=makeQuery(id+"F0.imprint","IMPRINT",FACE,{"disambiguationData":[TD([[makeQuery(id+"F0.imprint","IMPRINT",EDGE,{"derivedFrom":sQuery(id+"F0.wireOp",EDGE,"E110")}),-1.0]])]});
            var Q9;
            {var subQ4=sQuery(id+"F0.wireOp",EDGE,"E118");Q9=makeQuery(id+"F0.imprint","IMPRINT",FACE,{"disambiguationData":[TD([[makeQuery(id+"F0.imprint","IMPRINT",EDGE,{"derivedFrom":subQ4}),1.0]])]});}
            var Q10;
            Q10=makeQuery(id+"F0.imprint","IMPRINT",FACE,{"disambiguationData":[TD([[makeQuery(id+"F0.imprint","IMPRINT",EDGE,{"derivedFrom":sQuery(id+"F0.wireOp",EDGE,"E110")}),1.0]])]});
            var Q11;
            Q11=makeQuery(id+"F0.imprint","IMPRINT",FACE,{"disambiguationData":[TD([[makeQuery(id+"F0.imprint","IMPRINT",EDGE,{"derivedFrom":sQuery(id+"F0.wireOp",EDGE,"E127.sketch_text.stroke-0")}),-1.0]])]});
            var Q12;
            Q12=makeQuery(id+"F0.imprint","IMPRINT",FACE,{"disambiguationData":[TD([[makeQuery(id+"F0.imprint","IMPRINT",EDGE,{"derivedFrom":sQuery(id+"F0.wireOp",EDGE,"E129")}),-1.0]])]});
            var Q13;
            Q13=makeQuery(id+"F0.imprint","IMPRINT",FACE,{"disambiguationData":[TD([[makeQuery(id+"F0.imprint","IMPRINT",EDGE,{"derivedFrom":sQuery(id+"F0.wireOp",EDGE,"E146")}),-1.0]])]});
            var Q14;
            Q14=makeQuery(id+"F0.imprint","IMPRINT",FACE,{"disambiguationData":[TD([[makeQuery(id+"F0.imprint","IMPRINT",EDGE,{"derivedFrom":sQuery(id+"F0.wireOp",EDGE,"E129")}),1.0]])]});
            var Q15;
            {var subQ0=sQuery(id+"F0.wireOp",EDGE,"E134");var subQ1=sQuery(id+"F0.wireOp",EDGE,"E133");var subQ2=makeQuery(id+"F0.imprint","INTERSECT",VERTEX,{"derivedFrom":[subQ1,subQ0]});Q15=makeQuery(id+"F0.imprint","IMPRINT",FACE,{"disambiguationData":[TD([[makeQuery(id+"F0.imprint","IMPRINT",EDGE,{"disambiguationData":[TD([[subQ2,1.0]])],"derivedFrom":subQ1}),1.0]])]});}
            var Q16;
            Q16=makeQuery(id+"F0.imprint","IMPRINT",FACE,{"disambiguationData":[TD([[makeQuery(id+"F0.imprint","IMPRINT",EDGE,{"derivedFrom":sQuery(id+"F0.wireOp",EDGE,"E146")}),1.0]])]});
            extrude(context, id + "F3", {"entities" : qUnion([Q0, Q1, Q2, Q3, Q4, Q5, Q6, Q7, Q8, Q9, Q10, Q11, Q12, Q13, Q14, Q15, Q16]), "depth" : 1 * mm});
        }
        {
            var Q0;
            Q0=makeQuery(id+"F0.imprint","IMPRINT",FACE,{"disambiguationData":[TD([[makeQuery(id+"F0.imprint","IMPRINT",EDGE,{"derivedFrom":sQuery(id+"F0.wireOp",EDGE,"E27")}),1.0]])]});
            var Q1;
            {var subQ0=sQuery(id+"F0.wireOp",EDGE,"E100.left");Q1=makeQuery(id+"F0.imprint","IMPRINT",FACE,{"disambiguationData":[TD([[makeQuery(id+"F0.imprint","IMPRINT",EDGE,{"derivedFrom":subQ0}),-1.0]])]});}
            var Q2;
            {var subQ6=sQuery(id+"F0.wireOp",EDGE,"E89");Q2=makeQuery(id+"F0.imprint","IMPRINT",FACE,{"disambiguationData":[TD([[makeQuery(id+"F0.imprint","IMPRINT",EDGE,{"derivedFrom":subQ6}),1.0]])]});}
            var Q3;
            {var subQ5=sQuery(id+"F0.wireOp",EDGE,"E100.right");Q3=makeQuery(id+"F0.imprint","IMPRINT",FACE,{"disambiguationData":[TD([[makeQuery(id+"F0.imprint","IMPRINT",EDGE,{"derivedFrom":subQ5}),1.0]])]});}
            var Q4;
            {var subQ1=sQuery(id+"F0.wireOp",EDGE,"E91");Q4=makeQuery(id+"F0.imprint","IMPRINT",FACE,{"disambiguationData":[TD([[makeQuery(id+"F0.imprint","IMPRINT",EDGE,{"derivedFrom":subQ1}),1.0]])]});}
            var Q5;
            Q5=makeQuery(id+"F0.imprint","IMPRINT",FACE,{"disambiguationData":[TD([[makeQuery(id+"F0.imprint","IMPRINT",EDGE,{"derivedFrom":sQuery(id+"F0.wireOp",EDGE,"E110")}),1.0]])]});
            var Q6;
            Q6=makeQuery(id+"F0.imprint","IMPRINT",FACE,{"disambiguationData":[TD([[makeQuery(id+"F0.imprint","IMPRINT",EDGE,{"derivedFrom":sQuery(id+"F0.wireOp",EDGE,"E127.sketch_text.stroke-0")}),-1.0]])]});
            var Q7;
            Q7=makeQuery(id+"F0.imprint","IMPRINT",FACE,{"disambiguationData":[TD([[makeQuery(id+"F0.imprint","IMPRINT",EDGE,{"derivedFrom":sQuery(id+"F0.wireOp",EDGE,"E129")}),1.0]])]});
            var Q8;
            Q8=makeQuery(id+"F0.imprint","IMPRINT",FACE,{"disambiguationData":[TD([[makeQuery(id+"F0.imprint","IMPRINT",EDGE,{"derivedFrom":sQuery(id+"F0.wireOp",EDGE,"E145")}),1.0]])]});
            extrude(context, id + "F4", {"entities" : qUnion([Q0, Q1, Q2, Q3, Q4, Q5, Q6, Q7, Q8]), "operationType" : NewBodyOperationType.ADD, "depth" : 2 * mm});
        }
    });
